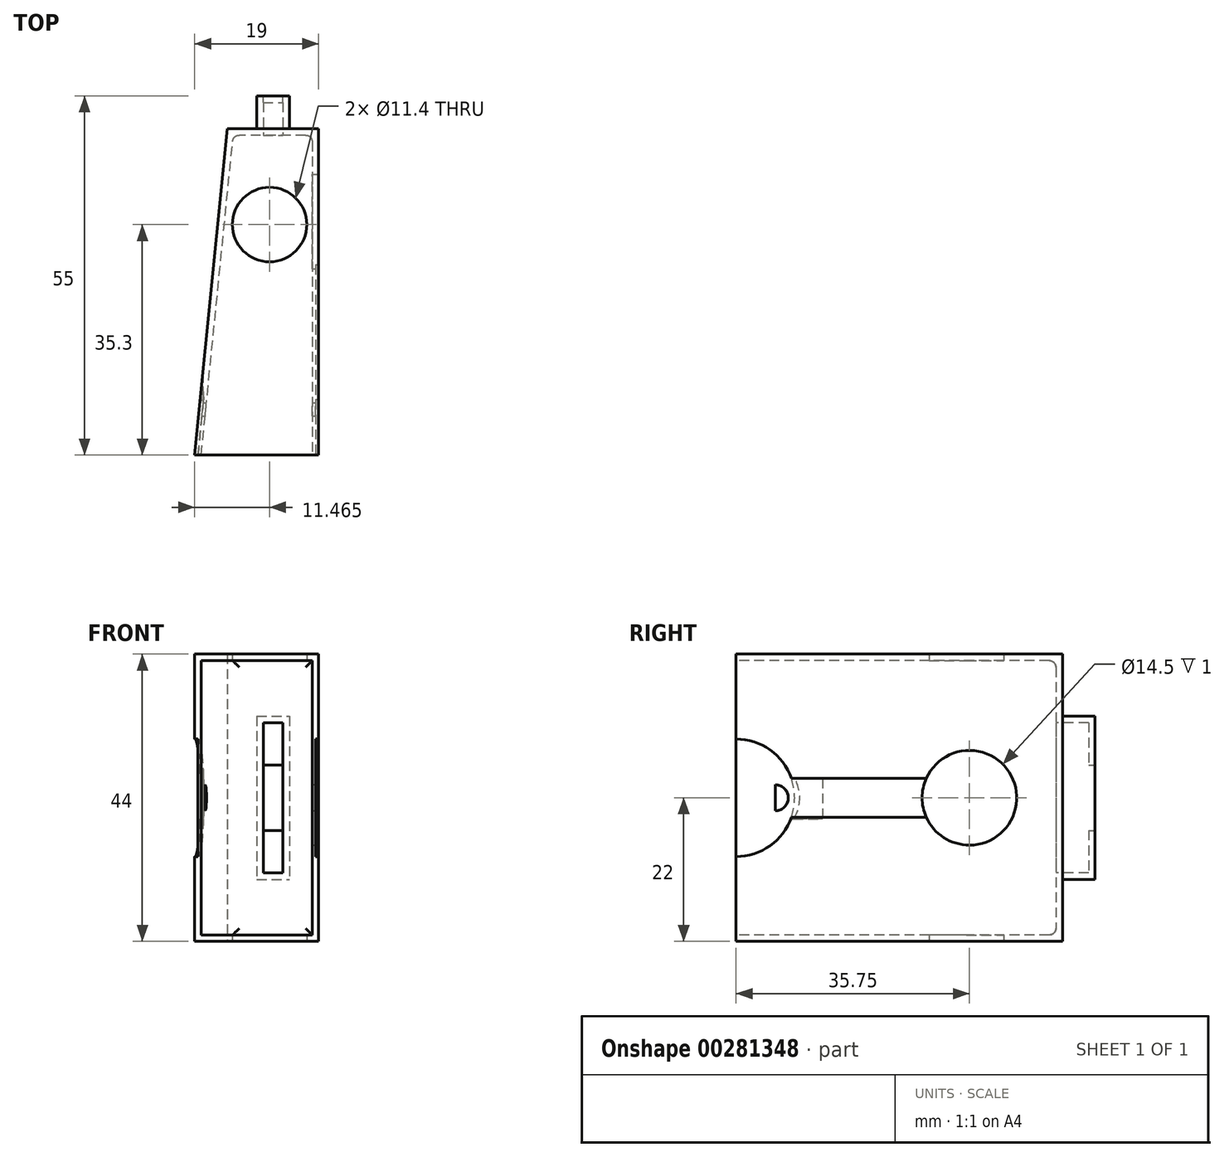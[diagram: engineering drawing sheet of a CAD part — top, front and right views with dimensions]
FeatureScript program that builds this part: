
annotation { "Feature Type Name" : "Feature", "Feature Type Description" : "" }
export const myFeature = defineFeature(function(context is Context, id is Id, definition is map)
    precondition{}
    {
        {
            var Q0;
            Q0=qCreatedBy(makeId("Top.planeOp"),FACE);
            var sketch = newSketch(context, id + "F0", { "sketchPlane" : qUnion([Q0])});
            skLineSegment(sketch, "E0.bottom", {"start": v(9.5, 37.5) * mm, "end": v(-4.5, 37.5) * mm});
            skLineSegment(sketch, "E0.left", {"start": v(9.5, 37.5) * mm, "end": v(9.5, -12.5) * mm});
            skPoint(sketch, "E0.middle", {"position": v(0, 0) * mm});
            skLineSegment(sketch, "E1", {"start": v(-9.5, -12.5) * mm, "end": v(-4.5, 37.5) * mm});
            skLineSegment(sketch, "E2", {"start": v(-9.5, -12.5) * mm, "end": v(9.5, -12.5) * mm});
            skSolve(sketch);
        }
        {
            var Q0;
            Q0=qSketchRegion(id+"F0",true);
            extrude(context, id + "F1", {"entities" : qUnion([Q0]), "depth" : 44 * mm});
        }
        {
            var Q0;
            Q0=makeQuery(id+"F1.opExtrude","SWEPT_FACE",FACE,{"disambiguationData":[OSD([sQuery(id+"F0.wireOp",EDGE,"E0.bottom")])]});
            var sketch = newSketch(context, id + "F2", { "sketchPlane" : qUnion([Q0])});
            skLineSegment(sketch, "E3.bottom", {"start": v(0, 34.5) * mm, "end": v(-5, 34.5) * mm});
            skLineSegment(sketch, "E3.top", {"start": v(0, 9.5) * mm, "end": v(-5, 9.5) * mm});
            skLineSegment(sketch, "E3.left", {"start": v(0, 34.5) * mm, "end": v(0, 9.5) * mm});
            skLineSegment(sketch, "E3.right", {"start": v(-5, 34.5) * mm, "end": v(-5, 9.5) * mm});
            skPoint(sketch, "E3.middle", {"position": v(-2.5, 22) * mm});
            skPoint(sketch, "E3.middle.positionSnap0", {"position": v(-9.5, 22) * mm});
            skPoint(sketch, "E3.middle.positionSnap1", {"position": v(-2.5, 44) * mm});
            skPoint(sketch, "E3.centerSnap0", {"position": v(-9.5, 22) * mm});
            skPoint(sketch, "E3.centerSnap1", {"position": v(-2.5, 44) * mm});
            skSolve(sketch);
        }
        {
            var Q0;
            Q0=makeQuery(id+"F2.imprint","IMPRINT",FACE,{"disambiguationData":[TD([[makeQuery(id+"F2.imprint","IMPRINT",EDGE,{"derivedFrom":sQuery(id+"F2.wireOp",EDGE,"E3.bottom")}),1.0]])]});
            extrude(context, id + "F3", {"entities" : qUnion([Q0]), "operationType" : NewBodyOperationType.ADD, "depth" : 5 * mm});
        }
        {
            var Q0;
            Q0=makeQuery(id+"F1.opExtrude","SWEPT_FACE",FACE,{"disambiguationData":[OSD([sQuery(id+"F0.wireOp",EDGE,"E2")])]});
            shell(context, id + "F4", {"entities" : qUnion([Q0]), "thickness" : 1 * mm});
        }
        {
            var Q0;
            Q0=makeQuery(id+"F1.opExtrude","CAP_FACE",FACE,{"disambiguationData":[OSD([sQuery(id+"F0.wireOp",EDGE,"E0.bottom"),sQuery(id+"F0.wireOp",EDGE,"E0.left"),sQuery(id+"F0.wireOp",EDGE,"E1"),sQuery(id+"F0.wireOp",EDGE,"E2")])],"isStart":true});
            var sketch = newSketch(context, id + "F5", { "sketchPlane" : qUnion([Q0])});
            skCircle(sketch, "E4", {"center": v(1.97, -22.8) * mm, "radius": 5.7 * mm});
            skSolve(sketch);
        }
        {
            var Q0;
            Q0=qSketchRegion(id+"F5",true);
            extrude(context, id + "F6", {"entities" : qUnion([Q0]), "operationType" : NewBodyOperationType.REMOVE, "endBound" : BoundingType.THROUGH_ALL, "oppositeDirection" : true, "depth" : 25 * mm});
        }
        {
            var Q0;
            Q0=makeQuery(id+"F3.opExtrude","CAP_FACE",FACE,{"disambiguationData":[OSD([sQuery(id+"F2.wireOp",EDGE,"E3.bottom"),sQuery(id+"F2.wireOp",EDGE,"E3.top"),sQuery(id+"F2.wireOp",EDGE,"E3.left"),sQuery(id+"F2.wireOp",EDGE,"E3.right")])],"isStart":false});
            var sketch = newSketch(context, id + "F7", { "sketchPlane" : qUnion([Q0])});
            skLineSegment(sketch, "E5.bottom", {"start": v(-1, 27) * mm, "end": v(-4, 27) * mm});
            skLineSegment(sketch, "E5.top", {"start": v(-1, 17) * mm, "end": v(-4, 17) * mm});
            skLineSegment(sketch, "E5.left", {"start": v(-1, 27) * mm, "end": v(-1, 17) * mm});
            skLineSegment(sketch, "E5.right", {"start": v(-4, 27) * mm, "end": v(-4, 17) * mm});
            skPoint(sketch, "E5.middle", {"position": v(-2.5, 22) * mm});
            skPoint(sketch, "E5.middle.positionSnap0", {"position": v(-5, 22) * mm});
            skPoint(sketch, "E5.middle.positionSnap1", {"position": v(-2.5, 34.5) * mm});
            skPoint(sketch, "E5.centerSnap0", {"position": v(-5, 22) * mm});
            skPoint(sketch, "E5.centerSnap1", {"position": v(-2.5, 34.5) * mm});
            skSolve(sketch);
        }
        {
            var Q0;
            Q0 = qSketchRegion(id + "F7", true);
            extrude(context, id + "F8", {"entities" : qUnion([Q0]), "operationType" : NewBodyOperationType.REMOVE, "oppositeDirection" : true, "depth" : 25 * mm});
        }
        {
            var Q0;
            Q0=makeQuery(id+"F1.opExtrude","SWEPT_FACE",FACE,{"disambiguationData":[OSD([sQuery(id+"F0.wireOp",EDGE,"E0.left")])]});
            var sketch = newSketch(context, id + "F9", { "sketchPlane" : qUnion([Q0])});
            skCircle(sketch, "E6", {"center": v(23.25, 22) * mm, "radius": 7.25 * mm});
            skPoint(sketch, "E6.centerSnap0", {"position": v(37.5, 22) * mm});
            skSolve(sketch);
        }
        {
            var Q0;
            Q0 = qSketchRegion(id + "F9", true);
            extrude(context, id + "F10", {"entities" : qUnion([Q0]), "operationType" : NewBodyOperationType.REMOVE, "oppositeDirection" : true, "depth" : 6.4 * mm});
        }
        {
            var Q0;
            Q0=makeQuery(id+"F1.opExtrude","SWEPT_FACE",FACE,{"disambiguationData":[OSD([sQuery(id+"F0.wireOp",EDGE,"E0.left")])]});
            var sketch = newSketch(context, id + "F11", { "sketchPlane" : qUnion([Q0])});
            skCircle(sketch, "E7", {"center": v(-12.5, 22) * mm, "radius": 9 * mm});
            skLineSegment(sketch, "E8.bottom", {"start": v(18.92, 24.98) * mm, "end": v(-7.6, 24.98) * mm});
            skLineSegment(sketch, "E8.top", {"start": v(18.92, 19.02) * mm, "end": v(-7.6, 19.02) * mm});
            skLineSegment(sketch, "E8.left", {"start": v(18.92, 24.98) * mm, "end": v(18.92, 19.02) * mm});
            skLineSegment(sketch, "E8.right", {"start": v(-7.6, 24.98) * mm, "end": v(-7.6, 19.02) * mm});
            skPoint(sketch, "E8.middle", {"position": v(5.66, 22) * mm});
            skSolve(sketch);
        }
        {
            var Q0;
            {var subQ0=sQuery(id+"F11.wireOp",EDGE,"E8.right");Q0=makeQuery(id+"F11.imprint","IMPRINT",FACE,{"disambiguationData":[TD([[makeQuery(id+"F11.imprint","IMPRINT",EDGE,{"derivedFrom":subQ0}),-1.0]])]});}
            var Q1;
            {var subQ5=sQuery(id+"F11.wireOp",EDGE,"E8.right");Q1=makeQuery(id+"F11.imprint","IMPRINT",FACE,{"disambiguationData":[TD([[makeQuery(id+"F11.imprint","IMPRINT",EDGE,{"derivedFrom":subQ5}),1.0]])]});}
            var Q2;
            {var subQ0=sQuery(id+"F11.wireOp",EDGE,"E8.bottom");var subQ1=sQuery(id+"F11.wireOp",EDGE,"E7");var subQ2=makeQuery(id+"F11.imprint","INTERSECT",VERTEX,{"derivedFrom":[subQ1,subQ0]});Q2=makeQuery(id+"F11.imprint","IMPRINT",FACE,{"disambiguationData":[TD([[makeQuery(id+"F11.imprint","IMPRINT",EDGE,{"disambiguationData":[TD([[subQ2,1.0]])],"derivedFrom":subQ1}),-1.0]])]});}
            extrude(context, id + "F12", {"entities" : qUnion([Q0, Q1, Q2]), "operationType" : NewBodyOperationType.REMOVE, "oppositeDirection" : true, "depth" : .5 * mm});
        }
        {
            var Q0;
            Q0=makeQuery(id+"F12.boolean.opBoolean","COPY",FACE,{"derivedFrom":makeQuery(id+"F12.opExtrude","CAP_FACE",FACE,{"disambiguationData":[OSD([sQuery(id+"F0.wireOp",EDGE,"E0.left"),sQuery(id+"F0.wireOp",EDGE,"E2"),sQuery(id+"F11.wireOp",EDGE,"E7")])],"isStart":false})});
            var sketch = newSketch(context, id + "F13", { "sketchPlane" : qUnion([Q0])});
            skPoint(sketch, "E9.middle", {"position": v(-6.5, 22) * mm});
            skPoint(sketch, "E9.middle.positionSnap0", {"position": v(-12.5, 22) * mm});
            skPoint(sketch, "E9.centerSnap0", {"position": v(-12.5, 22) * mm});
            skArc(sketch, "E10", {"start": v(-6.5, 20) * mm, "mid": v(-4.5, 22) * mm, "end": v(-6.5, 24) * mm});
            skLineSegment(sketch, "E11", {"start": v(-6.5, 24) * mm, "end": v(-6.5, 20) * mm});
            skSolve(sketch);
        }
        {
            var Q0;
            Q0=makeQuery(id+"F13.imprint","IMPRINT",FACE,{"disambiguationData":[TD([[makeQuery(id+"F13.imprint","IMPRINT",EDGE,{"derivedFrom":sQuery(id+"F13.wireOp",EDGE,"E10")}),1.0]])]});
            var Q1;
            Q1=sQuery(id+"F13.wireOp",EDGE,"E10");
            extrude(context, id + "F14", {"entities" : qUnion([Q0]), "operationType" : NewBodyOperationType.REMOVE, "surfaceEntities" : qUnion([Q1]), "oppositeDirection" : true, "depth" : 25 * mm});
        }
        {
            var Q0;
            Q0=makeQuery(id+"F1.opExtrude","SWEPT_FACE",FACE,{"disambiguationData":[OSD([sQuery(id+"F0.wireOp",EDGE,"E1")])]});
            var sketch = newSketch(context, id + "F15", { "sketchPlane" : qUnion([Q0])});
            skCircle(sketch, "E12", {"center": v(13.38, 22) * mm, "radius": 9 * mm});
            skSolve(sketch);
        }
        {
            var Q0;
            Q0 = qSketchRegion(id + "F15", true);
            extrude(context, id + "F16", {"entities" : qUnion([Q0]), "operationType" : NewBodyOperationType.REMOVE, "oppositeDirection" : true, "depth" : 0.5 * mm});
        }
        {
            var Q0;
            Q0=qCreatedBy(makeId("Front.planeOp"),FACE);
            var sketch = newSketch(context, id + "F17", { "sketchPlane" : qUnion([Q0])});
            skLineSegment(sketch, "E13.bottom", {"start": v(-8.18, 24.96) * mm, "end": v(-9.36, 24.96) * mm});
            skLineSegment(sketch, "E13.top", {"start": v(-8.18, 18.75) * mm, "end": v(-9.36, 18.75) * mm});
            skLineSegment(sketch, "E13.left", {"start": v(-8.18, 24.96) * mm, "end": v(-8.18, 18.75) * mm});
            skLineSegment(sketch, "E13.right", {"start": v(-9.36, 24.96) * mm, "end": v(-9.36, 18.75) * mm});
            skSolve(sketch);
        }
        {
            var Q0;
            Q0 = qSketchRegion(id + "F17", true);
            extrude(context, id + "F18", {"entities" : qUnion([Q0]), "operationType" : NewBodyOperationType.REMOVE, "endBound" : BoundingType.SYMMETRIC, "depth" : 8.42 * mm});
        }
        {
            var Q0;
            Q0=makeQuery(id+"F18.boolean.opBoolean","INTERSECT",EDGE,{"derivedFrom":[makeQuery(id+"F16.boolean.opBoolean","COPY",FACE,{"derivedFrom":makeQuery(id+"F16.opExtrude","SWEPT_FACE",FACE,{"disambiguationData":[OSD([sQuery(id+"F15.wireOp",EDGE,"E12")])]})}),makeQuery(id+"F18.opExtrude","SWEPT_FACE",FACE,{"disambiguationData":[OSD([sQuery(id+"F17.wireOp",EDGE,"E13.left")])]})]});
            fillet(context, id + "F19", {"entities" : qUnion([Q0]), "radius" : 5 * mm, "tangentPropagation" : true, "allowEdgeOverflow" : false});
        }
        {
            var Q0;
            {var subQ0=sQuery(id+"F0.wireOp",EDGE,"E0.bottom");Q0=makeQuery(id+"F4.opShell","OFFSET_EDGE",EDGE,{"disambiguationData":[OSD([subQ0]),TDD([makeQuery(id+"F1.opExtrude","CAP_EDGE",EDGE,{"disambiguationData":[OSD([subQ0])],"isStart":true})])]});}
            var Q1;
            {var subQ0=sQuery(id+"F0.wireOp",EDGE,"E0.bottom");Q1=makeQuery(id+"F4.opShell","OFFSET_EDGE",EDGE,{"disambiguationData":[OSD([subQ0]),TDD([makeQuery(id+"F1.opExtrude","CAP_EDGE",EDGE,{"disambiguationData":[OSD([subQ0])],"isStart":false})])]});}
            var Q2;
            Q2=makeQuery(id+"F4.opShell","OFFSET_EDGE",EDGE,{"disambiguationData":[OSD([sQuery(id+"F0.wireOp",EDGE,"E0.bottom"),sQuery(id+"F0.wireOp",EDGE,"E0.left")])]});
            var Q3;
            Q3=makeQuery(id+"F4.opShell","OFFSET_EDGE",EDGE,{"disambiguationData":[OSD([sQuery(id+"F0.wireOp",EDGE,"E0.bottom"),sQuery(id+"F0.wireOp",EDGE,"E1")])]});
            fillet(context, id + "F20", {"entities" : qUnion([Q0, Q1, Q2, Q3]), "radius" : 1 * mm, "tangentPropagation" : true, "allowEdgeOverflow" : false});
        }
    });
